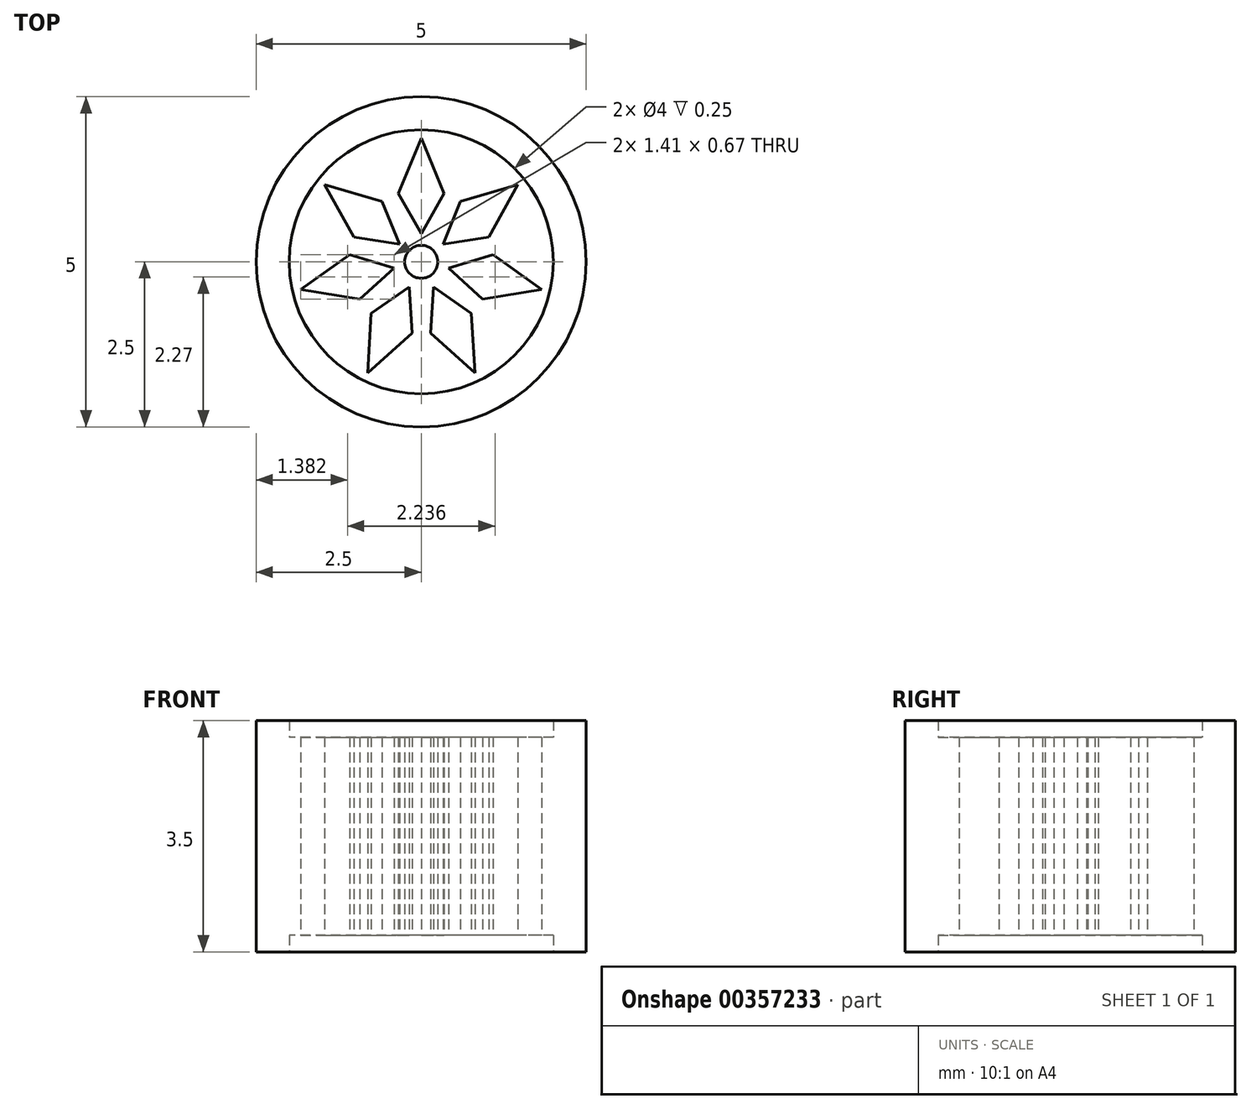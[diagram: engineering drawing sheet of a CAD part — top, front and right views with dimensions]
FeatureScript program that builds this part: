
annotation { "Feature Type Name" : "Feature", "Feature Type Description" : "" }
export const myFeature = defineFeature(function(context is Context, id is Id, definition is map)
    precondition{}
    {
        {
            var Q0;
            Q0=qCreatedBy(makeId("Top.planeOp"),FACE);
            var sketch = newSketch(context, id + "F0", { "sketchPlane" : qUnion([Q0])});
            skCircle(sketch, "E0", {"center": v(0, 0) * mm, "radius": 2 * mm});
            skCircle(sketch, "E1", {"center": v(0, 0) * mm, "radius": 0.25 * mm});
            skCircle(sketch, "E2", {"center": v(0, 0) * mm, "radius": 2.5 * mm});
            skLineSegment(sketch, "E3", {"start": v(0, 1.87) * mm, "end": v(-0.34, 1.03) * mm});
            skLineSegment(sketch, "E4", {"start": v(-0.34, 1.03) * mm, "end": v(0, 0.42) * mm});
            skLineSegment(sketch, "E5.MirrorCS", {"start": v(0.34, 1.03) * mm, "end": v(0, 0.42) * mm});
            skLineSegment(sketch, "E6.MirrorCS", {"start": v(0, 1.87) * mm, "end": v(0.34, 1.03) * mm});
            skLineSegment(sketch, "E7.1.1", {"start": v(-0.6, 0.91) * mm, "end": v(-0.33, 0.26) * mm});
            skLineSegment(sketch, "E7.1.2", {"start": v(-1.02, 0.38) * mm, "end": v(-0.33, 0.26) * mm});
            skLineSegment(sketch, "E7.1.3", {"start": v(-1.46, 1.17) * mm, "end": v(-1.02, 0.38) * mm});
            skLineSegment(sketch, "E7.1.4", {"start": v(-1.46, 1.17) * mm, "end": v(-0.6, 0.91) * mm});
            skLineSegment(sketch, "E7.2.1", {"start": v(-1.09, 0.1) * mm, "end": v(-0.41, -0.1) * mm});
            skLineSegment(sketch, "E7.2.2", {"start": v(-0.93, -0.57) * mm, "end": v(-0.41, -0.1) * mm});
            skLineSegment(sketch, "E7.2.3", {"start": v(-1.82, -0.42) * mm, "end": v(-0.93, -0.57) * mm});
            skLineSegment(sketch, "E7.2.4", {"start": v(-1.82, -0.42) * mm, "end": v(-1.09, 0.1) * mm});
            skLineSegment(sketch, "E7.3.1", {"start": v(-0.76, -0.78) * mm, "end": v(-0.18, -0.38) * mm});
            skLineSegment(sketch, "E7.3.2", {"start": v(-0.14, -1.08) * mm, "end": v(-0.18, -0.38) * mm});
            skLineSegment(sketch, "E7.3.3", {"start": v(-0.81, -1.69) * mm, "end": v(-0.14, -1.08) * mm});
            skLineSegment(sketch, "E7.3.4", {"start": v(-0.81, -1.69) * mm, "end": v(-0.76, -0.78) * mm});
            skLineSegment(sketch, "E7.4.1", {"start": v(0.14, -1.08) * mm, "end": v(0.18, -0.38) * mm});
            skLineSegment(sketch, "E7.4.2", {"start": v(0.76, -0.78) * mm, "end": v(0.18, -0.38) * mm});
            skLineSegment(sketch, "E7.4.3", {"start": v(0.81, -1.69) * mm, "end": v(0.76, -0.78) * mm});
            skLineSegment(sketch, "E7.4.4", {"start": v(0.81, -1.69) * mm, "end": v(0.14, -1.08) * mm});
            skLineSegment(sketch, "E7.5.1", {"start": v(0.93, -0.57) * mm, "end": v(0.41, -0.1) * mm});
            skLineSegment(sketch, "E7.5.2", {"start": v(1.09, 0.1) * mm, "end": v(0.41, -0.1) * mm});
            skLineSegment(sketch, "E7.5.3", {"start": v(1.82, -0.42) * mm, "end": v(1.09, 0.1) * mm});
            skLineSegment(sketch, "E7.5.4", {"start": v(1.82, -0.42) * mm, "end": v(0.93, -0.57) * mm});
            skLineSegment(sketch, "E7.6.1", {"start": v(1.02, 0.38) * mm, "end": v(0.33, 0.26) * mm});
            skLineSegment(sketch, "E7.6.2", {"start": v(0.6, 0.91) * mm, "end": v(0.33, 0.26) * mm});
            skLineSegment(sketch, "E7.6.3", {"start": v(1.46, 1.17) * mm, "end": v(0.6, 0.91) * mm});
            skLineSegment(sketch, "E7.6.4", {"start": v(1.46, 1.17) * mm, "end": v(1.02, 0.38) * mm});
            skSolve(sketch);
        }
        {
            var Q0;
            Q0=makeQuery(id+"F0.imprint","IMPRINT",FACE,{"disambiguationData":[TD([[makeQuery(id+"F0.imprint","IMPRINT",EDGE,{"derivedFrom":sQuery(id+"F0.wireOp",EDGE,"E0")}),1.0]])]});
            var Q1;
            Q1=makeQuery(id+"F0.imprint","IMPRINT",FACE,{"disambiguationData":[TD([[makeQuery(id+"F0.imprint","IMPRINT",EDGE,{"derivedFrom":sQuery(id+"F0.wireOp",EDGE,"E1")}),-1.0]])]});
            extrude(context, id + "F1", {"entities" : qUnion([Q0, Q1]), "endBound" : BoundingType.SYMMETRIC, "depth" : 3 * mm});
        }
        {
            var Q0;
            Q0 = qSketchRegion(id + "F0", true);
            extrude(context, id + "F2", {"entities" : qUnion([Q0]), "operationType" : NewBodyOperationType.ADD, "endBound" : BoundingType.SYMMETRIC, "depth" : 3.5 * mm});
        }
    });
